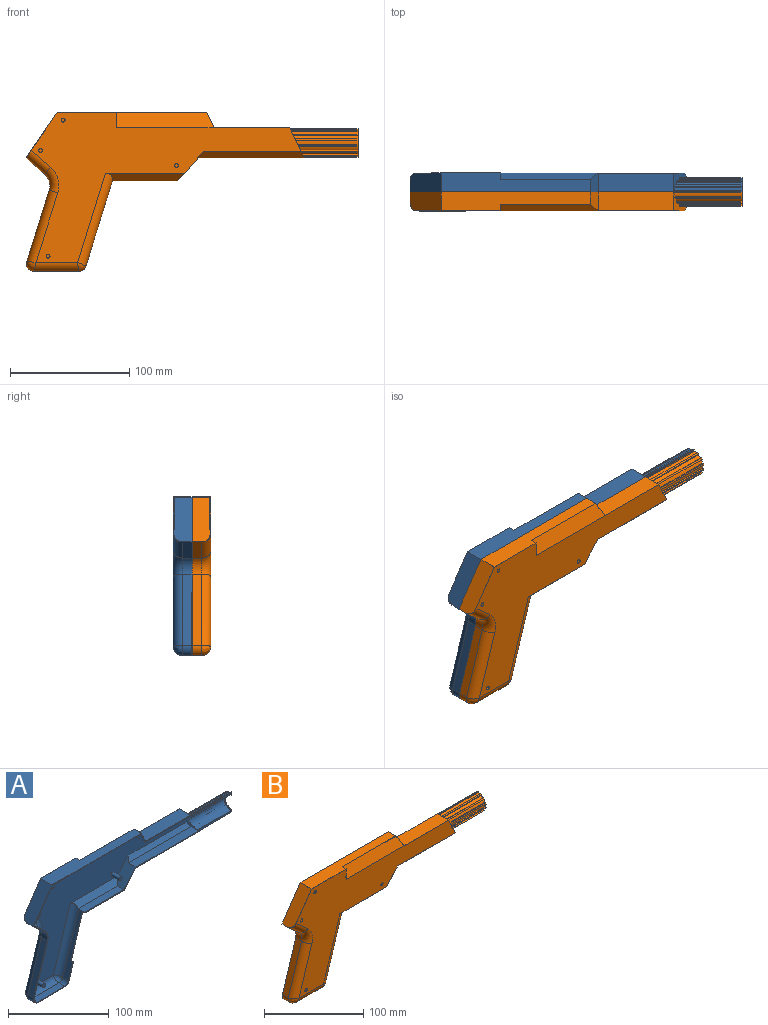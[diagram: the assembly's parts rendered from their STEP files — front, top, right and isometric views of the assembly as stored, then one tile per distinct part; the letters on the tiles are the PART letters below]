
ASSEMBLY  parts=2 mates=1
PART A: 100 faces, bbox 280.8x15.9x133.4 mm
  f0: plane 278.93x133.35mm, normal (0,-1,0), area 439.8mm2, adj f1,f3,f4,f5,f6,f7,f8,f9
  f1: plane 71.74x22.38mm, normal (0.95,0,-0.3), area 449mm2, adj f0,f10,f11,f31,f88,f89
  f2: plane 206.96x22.86mm, normal (0,-1,0), area 224.7mm2, adj f3,f4,f11,f12,f13,f18,f19,f60
  f3: plane 72.28x22.54mm, normal (-0.95,0,0.3), area 453.6mm2, adj f0,f2,f66,f67,f79,f88,f89,f90
  f4: plane 25.4x15.88mm, normal (0.91,0,0.42), area 214.1mm2, adj f0,f2,f13,f14,f19,f20,f21,f22
  f5: plane 125.84x15.88mm, normal (0,0,1), area 1576.7mm2, adj f0,f6,f15,f28,f29,f30
  f6: plane 15.88x12.7mm, normal (0.9,0,0.43), area 184.5mm2, adj f0,f5,f14,f29
  f7: plane 60.04x18.73mm, normal (-0.95,0,0.3), area 519.2mm2, adj f0,f8,f17,f35
  f8: cylinder r=6.35mm len=8.26mm, axis (0,1,0), area 98.2mm2, adj f0,f7,f9,f34
  f9: plane 37.5x8.26mm, normal (0,0,-1), area 309.5mm2, adj f0,f8,f10,f33
  f10: cylinder r=6.35mm len=8.26mm, axis (0,1,0), area 66.5mm2, adj f0,f1,f9,f32
  f11: plane 55.12x9.54mm, normal (0,0,-1), area 523.9mm2, adj f1,f2,f12,f31,f38,f90
  f12: plane 24.13x21.25mm, normal (0.75,0,-0.66), area 393.3mm2, adj f2,f11,f13,f28,f38,f39
  f13: plane 88.9x10.8mm, normal (0,0,-1), area 959.7mm2, adj f2,f4,f12,f39
  f14: plane 63.5x15.88mm, normal (0,0,1), area 1008.1mm2, adj f0,f4,f6,f28
  f15: plane 38.1x26.1mm, normal (-0.82,0,0.57), area 720.6mm2, adj f0,f5,f16,f28,f37
  f16: plane 15.64x13.61mm, normal (-0.66,0,-0.75), area 171.2mm2, adj f0,f15,f17,f37
  f17: cylinder r=12.7mm len=13.36mm, axis (0,1,0), area 121.3mm2, adj f0,f7,f16,f36
  f18: plane 24.08x11.91mm, normal (1,0,0), area 72.3mm2, adj f0,f2,f19,f20,f21,f22,f23,f24
  f19: plane 45.87x0.76mm, normal (0,0,-1), area 35mm2, adj f2,f4,f18,f40
  f20: plane 57.13x0.76mm, normal (0,0,1), area 43.5mm2, adj f0,f4,f18,f59
  f21: cylinder r=10.79mm len=56.54mm, axis (-1,0,0), area 187.2mm2, adj f4,f18,f58,f59
  f22: cylinder r=10.79mm len=55.88mm, axis (-1,0,0), area 184mm2, adj f4,f18,f55,f56
  f23: cylinder r=10.79mm len=54.36mm, axis (-1,0,0), area 178.2mm2, adj f4,f18,f52,f53
  f24: cylinder r=10.79mm len=52.27mm, axis (-1,0,0), area 171mm2, adj f4,f18,f49,f50
  f25: cylinder r=10.79mm len=50.03mm, axis (-1,0,0), area 163.7mm2, adj f4,f18,f46,f47
  f26: cylinder r=10.79mm len=48.08mm, axis (-1,0,0), area 157.9mm2, adj f4,f18,f43,f44
  f27: cylinder r=10.79mm len=46.81mm, axis (-1,0,0), area 154.7mm2, adj f4,f18,f40,f41
  f28: plane 226.67x125.73mm, normal (0,1,0), area 9946.1mm2, adj f4,f5,f12,f14,f15,f29,f30,f31
  f29: plane 82.26x12.7mm, normal (0,0.92,0.4), area 1097.3mm2, adj f5,f6,f28,f30
  f30: plane 12.7x5.52mm, normal (1,0,0), area 35.1mm2, adj f5,f28,f29
  f31: cylinder r=7.62mm len=78.42mm, axis (0.3,0,0.95), area 930.8mm2, adj f1,f11,f28,f32,f38
  f32: bspline ~9.05x7.62mm, area 62mm2, adj f10,f31,f33
  f33: cylinder r=7.62mm len=37.5mm, axis (1,0,0), area 437.2mm2, adj f9,f28,f32,f34
  f34: bspline ~10.36x10.14mm, area 93.3mm2, adj f8,f33,f35
  f35: cylinder r=7.62mm len=62.31mm, axis (-0.3,0,-0.95), area 745.3mm2, adj f7,f28,f34,f36
  f36: torus R=20.32mm, axis (0,-1,0), area 214.3mm2, adj f17,f28,f35,f37
  f37: cylinder r=7.62mm len=21.31mm, axis (0.75,0,-0.66), area 252mm2, adj f15,f16,f28,f36
  f38: plane 66.59x6.35mm, normal (0,0.71,-0.71), area 528.5mm2, adj f11,f12,f28,f31
  f39: plane 88.9x5.08mm, normal (0,0.71,-0.71), area 614.1mm2, adj f4,f12,f13,f28
  f40: plane 46.46x1.27mm, normal (0,1,0), area 58.6mm2, adj f4,f18,f19,f27
  f41: plane 46.81x1.14mm, normal (0,-0.9,-0.43), area 59.1mm2, adj f4,f18,f27,f42
  f42: plane 46.58x1.37mm, normal (0,0.43,-0.9), area 70.8mm2, adj f4,f18,f41,f43
  f43: plane 47.11x1.14mm, normal (0,0.9,0.43), area 59.5mm2, adj f4,f18,f26,f42
  f44: plane 48.08x0.99mm, normal (0,-0.62,-0.78), area 60.8mm2, adj f4,f18,f26,f45
  f45: plane 48.27x1.19mm, normal (0,0.78,-0.62), area 73.1mm2, adj f4,f18,f44,f46
  f46: plane 48.64x0.99mm, normal (0,0.62,0.78), area 61.5mm2, adj f4,f18,f25,f45
  f47: plane 50.03x1.24mm, normal (0,-0.22,-0.97), area 63.5mm2, adj f4,f18,f25,f48
  f48: plane 50.59x1.49mm, normal (0,0.97,-0.22), area 76.6mm2, adj f4,f18,f47,f49
  f49: plane 50.73x1.24mm, normal (0,0.22,0.97), area 64.3mm2, adj f4,f18,f24,f48
  f50: plane 52.41x1.24mm, normal (0,0.22,-0.97), area 66.5mm2, adj f4,f18,f24,f51
  f51: plane 53.1x1.49mm, normal (0,0.97,0.22), area 80.4mm2, adj f4,f18,f50,f52
  f52: plane 53.1x1.24mm, normal (0,-0.22,0.97), area 67.4mm2, adj f4,f18,f23,f51
  f53: plane 54.73x0.99mm, normal (0,0.62,-0.78), area 69.3mm2, adj f4,f18,f23,f54
  f54: plane 55.29x1.19mm, normal (0,0.78,0.62), area 83.8mm2, adj f4,f18,f53,f55
  f55: plane 55.29x0.99mm, normal (0,-0.62,0.78), area 70mm2, adj f4,f18,f22,f54
  f56: plane 56.42x1.14mm, normal (0,0.9,-0.43), area 71.3mm2, adj f4,f18,f22,f57
  f57: plane 56.73x1.37mm, normal (0,0.43,0.9), area 86.2mm2, adj f4,f18,f56,f58
  f58: plane 56.73x1.14mm, normal (0,-0.9,0.43), area 71.7mm2, adj f4,f18,f21,f57
  f59: plane 57.13x1.27mm, normal (0,1,0), area 72.2mm2, adj f4,f18,f20,f21
  f60: plane 23.88x15.11mm, normal (-0.91,0,-0.42), area 212mm2, adj f0,f2,f69,f70,f75,f76,f87
  f61: plane 124.95x15.11mm, normal (0,0,-1), area 1486mm2, adj f0,f62,f71,f76,f77,f78
  f62: plane 15.11x12.7mm, normal (-0.9,0,-0.43), area 177.4mm2, adj f0,f61,f70,f76,f77
  f63: plane 60.04x18.73mm, normal (0.95,0,-0.3), area 519.2mm2, adj f0,f64,f73,f83
  f64: cylinder r=5.59mm len=8.26mm, axis (0,1,0), area 86.4mm2, adj f0,f63,f65,f82
  f65: plane 37.5x8.26mm, normal (0,0,1), area 309.5mm2, adj f0,f64,f66,f81
  f66: cylinder r=5.59mm len=8.26mm, axis (0,1,0), area 58.5mm2, adj f0,f3,f65,f80
  f67: plane 55.29x9.22mm, normal (0,0,1), area 508.5mm2, adj f2,f3,f68,f79,f86
  f68: plane 23.68x20.86mm, normal (-0.75,0,0.66), area 374.7mm2, adj f2,f67,f69,f76,f86,f87
  f69: plane 88.05x10.48mm, normal (0,0,1), area 922.7mm2, adj f2,f60,f68,f87
  f70: plane 63.5x15.11mm, normal (0,0,-1), area 959.6mm2, adj f0,f60,f62,f76
  f71: plane 37.21x25.49mm, normal (0.82,0,-0.57), area 671.5mm2, adj f0,f61,f72,f76,f85
  f72: plane 15.13x13.16mm, normal (0.66,0,0.75), area 165.5mm2, adj f0,f71,f73,f85
  f73: cylinder r=13.46mm len=14.17mm, axis (0,1,0), area 128.6mm2, adj f0,f63,f72,f84
  f74: plane 20.07x10.03mm, normal (-1,0,0), area 34mm2, adj f0,f2,f75,f99
  f75: cylinder r=10.03mm len=56.27mm, axis (-1,0,0), area 1625.7mm2, adj f0,f2,f60,f74
  f76: plane 225.1x124.97mm, normal (0,-1,0), area 9664.9mm2, adj f60,f61,f62,f68,f70,f71,f77,f78
  f77: plane 82.25x12.1mm, normal (0,-0.92,-0.4), area 1047mm2, adj f61,f62,f76,f78
  f78: plane 12.1x5.26mm, normal (-1,0,0), area 31.8mm2, adj f61,f76,f77
  f79: cylinder r=6.86mm len=78.48mm, axis (0.3,0,0.95), area 842.5mm2, adj f3,f67,f76,f80,f86
  f80: bspline ~8.14x6.86mm, area 49.1mm2, adj f66,f79,f81
  f81: cylinder r=6.86mm len=37.5mm, axis (1,0,0), area 393.5mm2, adj f65,f76,f80,f82
  f82: bspline ~9.32x9.08mm, area 74.1mm2, adj f64,f81,f83
  f83: cylinder r=6.86mm len=62.08mm, axis (-0.3,0,-0.95), area 670.7mm2, adj f63,f76,f82,f84
  f84: torus R=20.32mm, axis (0,-1,0), area 198.9mm2, adj f73,f76,f83,f85
  f85: cylinder r=6.86mm len=20.23mm, axis (0.75,0,-0.66), area 219.1mm2, adj f71,f72,f76,f84
  f86: plane 65.75x5.9mm, normal (0,-0.71,0.71), area 489.9mm2, adj f67,f68,f76,f79
  f87: plane 88.05x4.63mm, normal (0,-0.71,0.71), area 556.5mm2, adj f60,f68,f69,f76
  f88: plane 3.18x0.73mm, normal (0.3,0,0.95), area 2.4mm2, adj f0,f1,f3,f89
  f89: plane 51.75x16.8mm, normal (0,-1,0), area 41.1mm2, adj f1,f3,f88,f90
  f90: plane 3.18x0.73mm, normal (-0.3,0,-0.95), area 2.4mm2, adj f2,f3,f11,f89
  f91: cylinder r=2.22mm len=11.43mm, axis (0,1,0), area 159.7mm2, adj f76,f92
  f92: plane 4.45x4.45mm, normal (0,-1,0), area 15.5mm2, adj f91
  f93: cylinder r=2.22mm len=11.43mm, axis (0,1,0), area 159.6mm2, adj f76,f94
  f94: plane 4.45x4.45mm, normal (0,-1,0), area 15.5mm2, adj f93
  f95: cylinder r=2.22mm len=11.43mm, axis (0,1,0), area 159.6mm2, adj f76,f96
  f96: plane 4.45x4.45mm, normal (0,-1,0), area 15.5mm2, adj f95
  f97: cylinder r=2.22mm len=11.43mm, axis (0,1,0), area 159.6mm2, adj f76,f98
  f98: plane 4.45x4.45mm, normal (0,-1,0), area 15.5mm2, adj f97
  f99: cylinder r=8.89mm len=17.78mm, axis (1,0,0), area 21.3mm2, adj f0,f2,f18,f74
PART B: 108 faces, bbox 280.8x19.1x133.4 mm
  f0: plane 278.93x133.35mm, normal (0,1,0), area 439.8mm2, adj f1,f2,f10,f11,f12,f13,f14,f15
  f1: plane 71.74x22.38mm, normal (0.95,0,-0.3), area 449mm2, adj f0,f16,f17,f34,f88,f89
  f2: plane 72.28x22.54mm, normal (-0.95,0,0.3), area 453.6mm2, adj f0,f59,f67,f68,f85,f88,f89,f90
  f3: cylinder r=10.79mm len=46.81mm, axis (-1,0,0), area 154.7mm2, adj f10,f25,f37,f58
  f4: cylinder r=10.79mm len=48.08mm, axis (-1,0,0), area 157.9mm2, adj f10,f25,f55,f56
  f5: cylinder r=10.79mm len=50.03mm, axis (-1,0,0), area 163.7mm2, adj f10,f25,f52,f53
  f6: cylinder r=10.79mm len=52.27mm, axis (-1,0,0), area 171mm2, adj f10,f25,f49,f50
  f7: cylinder r=10.79mm len=54.36mm, axis (-1,0,0), area 178.2mm2, adj f10,f25,f46,f47
  f8: cylinder r=10.79mm len=55.88mm, axis (-1,0,0), area 184mm2, adj f10,f25,f43,f44
  f9: cylinder r=10.79mm len=56.54mm, axis (-1,0,0), area 187.2mm2, adj f10,f25,f40,f41
  f10: plane 25.4x15.88mm, normal (0.91,0,0.42), area 214.1mm2, adj f0,f3,f4,f5,f6,f7,f8,f9
  f11: plane 125.84x15.88mm, normal (0,0,1), area 1576.7mm2, adj f0,f12,f21,f24,f26,f27
  f12: plane 15.88x12.7mm, normal (0.9,0,0.43), area 184.5mm2, adj f0,f11,f20,f26
  f13: plane 60.04x18.73mm, normal (-0.95,0,0.3), area 519.2mm2, adj f0,f14,f23,f30
  f14: cylinder r=6.35mm len=8.26mm, axis (0,1,0), area 98.2mm2, adj f0,f13,f15,f31
  f15: plane 37.5x8.26mm, normal (0,0,-1), area 309.5mm2, adj f0,f14,f16,f32
  f16: cylinder r=6.35mm len=8.26mm, axis (0,1,0), area 66.5mm2, adj f0,f1,f15,f33
  f17: plane 55.12x9.54mm, normal (0,0,-1), area 523.9mm2, adj f1,f18,f34,f35,f59,f90
  f18: plane 24.13x21.25mm, normal (0.75,0,-0.66), area 393.3mm2, adj f17,f19,f24,f35,f36,f59
  f19: plane 88.9x10.8mm, normal (0,0,-1), area 959.7mm2, adj f10,f18,f36,f59
  f20: plane 63.5x15.88mm, normal (0,0,1), area 1008.1mm2, adj f0,f10,f12,f24
  f21: plane 38.1x26.1mm, normal (-0.82,0,0.57), area 720.6mm2, adj f0,f11,f22,f24,f28
  f22: plane 15.64x13.61mm, normal (-0.66,0,-0.75), area 171.2mm2, adj f0,f21,f23,f28
  f23: cylinder r=12.7mm len=13.36mm, axis (0,1,0), area 121.3mm2, adj f0,f13,f22,f29
  f24: plane 226.67x125.73mm, normal (0,-1,0), area 9914.5mm2, adj f10,f11,f18,f20,f21,f26,f27,f28
  f25: plane 24.08x11.91mm, normal (1,0,0), area 72.3mm2, adj f0,f3,f4,f5,f6,f7,f8,f9
  f26: plane 82.26x12.7mm, normal (0,-0.92,0.4), area 1097.3mm2, adj f11,f12,f24,f27
  f27: plane 12.7x5.52mm, normal (1,0,0), area 35.1mm2, adj f11,f24,f26
  f28: cylinder r=7.62mm len=21.31mm, axis (-0.75,0,0.66), area 252mm2, adj f21,f22,f24,f29
  f29: torus R=20.32mm, axis (0,-1,0), area 214.3mm2, adj f23,f24,f28,f30
  f30: cylinder r=7.62mm len=62.31mm, axis (0.3,0,0.95), area 745.3mm2, adj f13,f24,f29,f31
  f31: bspline ~10.36x10.14mm, area 93.3mm2, adj f14,f30,f32
  f32: cylinder r=7.62mm len=37.5mm, axis (-1,0,0), area 437.2mm2, adj f15,f24,f31,f33
  f33: bspline ~9.05x7.62mm, area 62mm2, adj f16,f32,f34
  f34: cylinder r=7.62mm len=78.42mm, axis (-0.3,0,-0.95), area 930.8mm2, adj f1,f17,f24,f33,f35
  f35: plane 66.59x6.35mm, normal (0,-0.71,-0.71), area 528.5mm2, adj f17,f18,f24,f34
  f36: plane 88.9x5.08mm, normal (0,-0.71,-0.71), area 614.1mm2, adj f10,f18,f19,f24
  f37: plane 46.46x1.27mm, normal (0,-1,0), area 58.6mm2, adj f3,f10,f25,f38
  f38: plane 45.87x0.76mm, normal (0,0,-1), area 35mm2, adj f10,f25,f37,f59
  f39: plane 57.13x0.76mm, normal (0,0,1), area 43.5mm2, adj f0,f10,f25,f40
  f40: plane 57.13x1.27mm, normal (0,-1,0), area 72.2mm2, adj f9,f10,f25,f39
  f41: plane 56.73x1.14mm, normal (0,0.9,0.43), area 71.7mm2, adj f9,f10,f25,f42
  f42: plane 56.73x1.37mm, normal (0,-0.43,0.9), area 86.2mm2, adj f10,f25,f41,f43
  f43: plane 56.42x1.14mm, normal (0,-0.9,-0.43), area 71.3mm2, adj f8,f10,f25,f42
  f44: plane 55.29x0.99mm, normal (0,0.62,0.78), area 70mm2, adj f8,f10,f25,f45
  f45: plane 55.29x1.19mm, normal (0,-0.78,0.62), area 83.8mm2, adj f10,f25,f44,f46
  f46: plane 54.73x0.99mm, normal (0,-0.62,-0.78), area 69.3mm2, adj f7,f10,f25,f45
  f47: plane 53.1x1.24mm, normal (0,0.22,0.97), area 67.4mm2, adj f7,f10,f25,f48
  f48: plane 53.1x1.49mm, normal (0,-0.97,0.22), area 80.4mm2, adj f10,f25,f47,f49
  f49: plane 52.41x1.24mm, normal (0,-0.22,-0.97), area 66.5mm2, adj f6,f10,f25,f48
  f50: plane 50.73x1.24mm, normal (0,-0.22,0.97), area 64.3mm2, adj f6,f10,f25,f51
  f51: plane 50.59x1.49mm, normal (0,-0.97,-0.22), area 76.6mm2, adj f10,f25,f50,f52
  f52: plane 50.03x1.24mm, normal (0,0.22,-0.97), area 63.5mm2, adj f5,f10,f25,f51
  f53: plane 48.64x0.99mm, normal (0,-0.62,0.78), area 61.5mm2, adj f5,f10,f25,f54
  f54: plane 48.27x1.19mm, normal (0,-0.78,-0.62), area 73.1mm2, adj f10,f25,f53,f55
  f55: plane 48.08x0.99mm, normal (0,0.62,-0.78), area 60.8mm2, adj f4,f10,f25,f54
  f56: plane 47.11x1.14mm, normal (0,-0.9,0.43), area 59.5mm2, adj f4,f10,f25,f57
  f57: plane 46.58x1.37mm, normal (0,-0.43,-0.9), area 70.8mm2, adj f10,f25,f56,f58
  f58: plane 46.81x1.14mm, normal (0,0.9,-0.43), area 59.1mm2, adj f3,f10,f25,f57
  f59: plane 206.96x22.86mm, normal (0,1,0), area 224.7mm2, adj f2,f10,f17,f18,f19,f25,f38,f60
  f60: cylinder r=10.03mm len=56.27mm, axis (-1,0,0), area 1625.7mm2, adj f0,f59,f61,f76
  f61: plane 23.88x15.11mm, normal (-0.91,0,-0.42), area 212mm2, adj f0,f59,f60,f70,f71,f75,f87
  f62: plane 124.95x15.11mm, normal (0,0,-1), area 1486mm2, adj f0,f63,f72,f75,f77,f78
  f63: plane 15.11x12.7mm, normal (-0.9,0,-0.43), area 177.4mm2, adj f0,f62,f71,f75,f77
  f64: plane 60.04x18.73mm, normal (0.95,0,-0.3), area 519.2mm2, adj f0,f65,f74,f81
  f65: cylinder r=5.59mm len=8.26mm, axis (0,1,0), area 86.4mm2, adj f0,f64,f66,f82
  f66: plane 37.5x8.26mm, normal (0,0,1), area 309.5mm2, adj f0,f65,f67,f83
  f67: cylinder r=5.59mm len=8.26mm, axis (0,1,0), area 58.5mm2, adj f0,f2,f66,f84
  f68: plane 55.29x9.22mm, normal (0,0,1), area 508.5mm2, adj f2,f59,f69,f85,f86
  f69: plane 23.68x20.86mm, normal (-0.75,0,0.66), area 374.7mm2, adj f59,f68,f70,f75,f86,f87
  f70: plane 88.05x10.48mm, normal (0,0,1), area 922.7mm2, adj f59,f61,f69,f87
  f71: plane 63.5x15.11mm, normal (0,0,-1), area 959.6mm2, adj f0,f61,f63,f75
  f72: plane 37.21x25.49mm, normal (0.82,0,-0.57), area 671.5mm2, adj f0,f62,f73,f75,f79
  f73: plane 15.13x13.16mm, normal (0.66,0,0.75), area 165.5mm2, adj f0,f72,f74,f79
  f74: cylinder r=13.46mm len=14.17mm, axis (0,1,0), area 128.6mm2, adj f0,f64,f73,f80
  f75: plane 225.1x124.97mm, normal (0,1,0), area 9664.9mm2, adj f61,f62,f63,f69,f71,f72,f77,f78
  f76: plane 20.07x10.03mm, normal (-1,0,0), area 34mm2, adj f0,f59,f60,f99
  f77: plane 82.25x12.1mm, normal (0,0.92,-0.4), area 1047mm2, adj f62,f63,f75,f78
  f78: plane 12.1x5.26mm, normal (-1,0,0), area 31.8mm2, adj f62,f75,f77
  f79: cylinder r=6.86mm len=20.23mm, axis (-0.75,0,0.66), area 219.1mm2, adj f72,f73,f75,f80
  f80: torus R=20.32mm, axis (0,-1,0), area 198.9mm2, adj f74,f75,f79,f81
  f81: cylinder r=6.86mm len=62.08mm, axis (0.3,0,0.95), area 670.7mm2, adj f64,f75,f80,f82
  f82: bspline ~9.32x9.08mm, area 74.1mm2, adj f65,f81,f83
  f83: cylinder r=6.86mm len=37.5mm, axis (-1,0,0), area 393.5mm2, adj f66,f75,f82,f84
  f84: bspline ~8.14x6.86mm, area 49.1mm2, adj f67,f83,f85
  f85: cylinder r=6.86mm len=78.48mm, axis (-0.3,0,-0.95), area 842.5mm2, adj f2,f68,f75,f84,f86
  f86: plane 65.75x5.9mm, normal (0,0.71,0.71), area 489.9mm2, adj f68,f69,f75,f85
  f87: plane 88.05x4.63mm, normal (0,0.71,0.71), area 556.5mm2, adj f61,f69,f70,f75
  f88: plane 51.75x16.8mm, normal (0,1,0), area 41.1mm2, adj f1,f2,f89,f90
  f89: plane 3.18x0.73mm, normal (0.3,0,0.95), area 2.4mm2, adj f0,f1,f2,f88
  f90: plane 3.18x0.73mm, normal (-0.3,0,-0.95), area 2.4mm2, adj f2,f17,f59,f88
  f91: cylinder r=2.22mm len=18.29mm, axis (0,-1,0), area 255.6mm2, adj f75,f92
  f92: plane 4.45x4.45mm, normal (0,1,0), area 15.5mm2, adj f91
  f93: cylinder r=2.22mm len=18.29mm, axis (0,-1,0), area 255.4mm2, adj f75,f94
  f94: plane 4.45x4.45mm, normal (0,1,0), area 15.5mm2, adj f93
  f95: cylinder r=2.22mm len=18.29mm, axis (0,-1,0), area 255.4mm2, adj f75,f96
  f96: plane 4.45x4.45mm, normal (0,1,0), area 15.5mm2, adj f95
  f97: cylinder r=2.22mm len=18.29mm, axis (0,-1,0), area 255.4mm2, adj f75,f98
  f98: plane 4.45x4.45mm, normal (0,1,0), area 15.5mm2, adj f97
  f99: cylinder r=8.89mm len=17.78mm, axis (1,0,0), area 21.3mm2, adj f0,f25,f59,f76
  f100: cylinder r=1.59mm len=16.51mm, axis (0,-1,0), area 164.7mm2, adj f24,f101
  f101: plane 3.18x3.18mm, normal (0,-1,0), area 7.9mm2, adj f100
  f102: cylinder r=1.59mm len=16.51mm, axis (0,-1,0), area 164.7mm2, adj f24,f103
  f103: plane 3.18x3.18mm, normal (0,-1,0), area 7.9mm2, adj f102
  f104: cylinder r=1.59mm len=16.51mm, axis (0,-1,0), area 164.7mm2, adj f24,f105
  f105: plane 3.18x3.18mm, normal (0,-1,0), area 7.9mm2, adj f104
  f106: cylinder r=1.59mm len=16.51mm, axis (0,-1,0), area 164.7mm2, adj f24,f107
  f107: plane 3.18x3.18mm, normal (0,-1,0), area 7.9mm2, adj f106
PLACE A t=(12.5,8.54,10.4)mm
PLACE B t=(12.5,135.03,10.4)mm
MATE fastened B.f0 <-> A.f0  axis (0,1,0) through (-139.44,-7.34,29.45)mm
